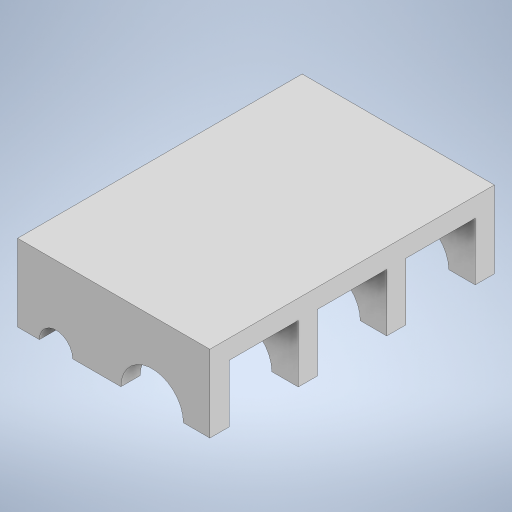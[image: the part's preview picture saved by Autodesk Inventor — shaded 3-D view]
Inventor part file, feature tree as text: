
AUTODESK INVENTOR PART (.ipt)
format: ipt  version: 2023 (Build 270158000, 158)  size: 264,192 bytes
history: native  units: in
note: dims shown in document units (in); Inventor stores cm internally (conversion verified against a paired STEP export)
features: extrude x2, sketch x1
ambient origin geometry x8: Origin, YZ Plane, XZ Plane, XY Plane, X Axis, Y Axis, Z Axis, Center Point
bodies: Solid1 (feature_tree)
feature tree (3):
  extrude  "Extrusion1"  Depth=0.5in
  extrude  "Extrusion2"  Depth=7.4in TaperAngle=0.0deg
  sketch  "Sketch1"  dims[d0=5.0in d2=1.625in d3=7.4in d4=0.0in d15=1.4in d16=3.7in d17=6.0in d18=0.5in d20=2.528in d21=7.4in d22=0.0in d25=1.5in d26=0.866in d31=1.2546in d32=0.5669in d33=2.0in d34=1.5in d27=0.5in d28=0.0344in d29=0.0in d30=0.0in]
